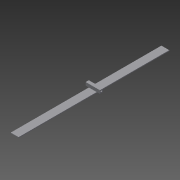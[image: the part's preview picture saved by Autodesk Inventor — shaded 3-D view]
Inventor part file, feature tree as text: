
AUTODESK INVENTOR PART (.ipt)
format: ipt  version: 2014 SP1 (Build 180222100, 222)  size: 89,600 bytes
history: native  units: mm
features: sketch x4, extrude x3, plane x1, projected_geometry x1
ambient origin geometry x8: Origin, YZ Plane, XZ Plane, XY Plane, X Axis, Y Axis, Z Axis, Center Point
bodies: Solid1 (feature_tree)
feature tree (9):
  extrude  "Extrusion1"  Depth=5.0mm
  plane  "Work Plane1"
  sketch  "Sketch3"  dims[d2=955.0mm d3=0.0mm d17=0.0mm]
  sketch  "Sketch5"  dims[d33=20.0mm d37=20.0mm d38=0.0mm]
  extrude  "Extrusion7"  TaperAngle=0.0deg  [1 undecoded]
  extrude  "Extrusion8"  Depth=20.0mm TaperAngle=0.0deg
  sketch  "Sketch1"  dims[d0=50.0mm d1=5.0mm]
  projected_geometry  "Projected Loop1"
  sketch  "Sketch7"  dims[d39=10.0mm d40=100.0mm d41=0.0mm]
note: 1 required parameter value undecoded (feature->parameter linkage not recoverable at this tier; creation-order binding heuristic only, values carry confidence <= 0.55)
